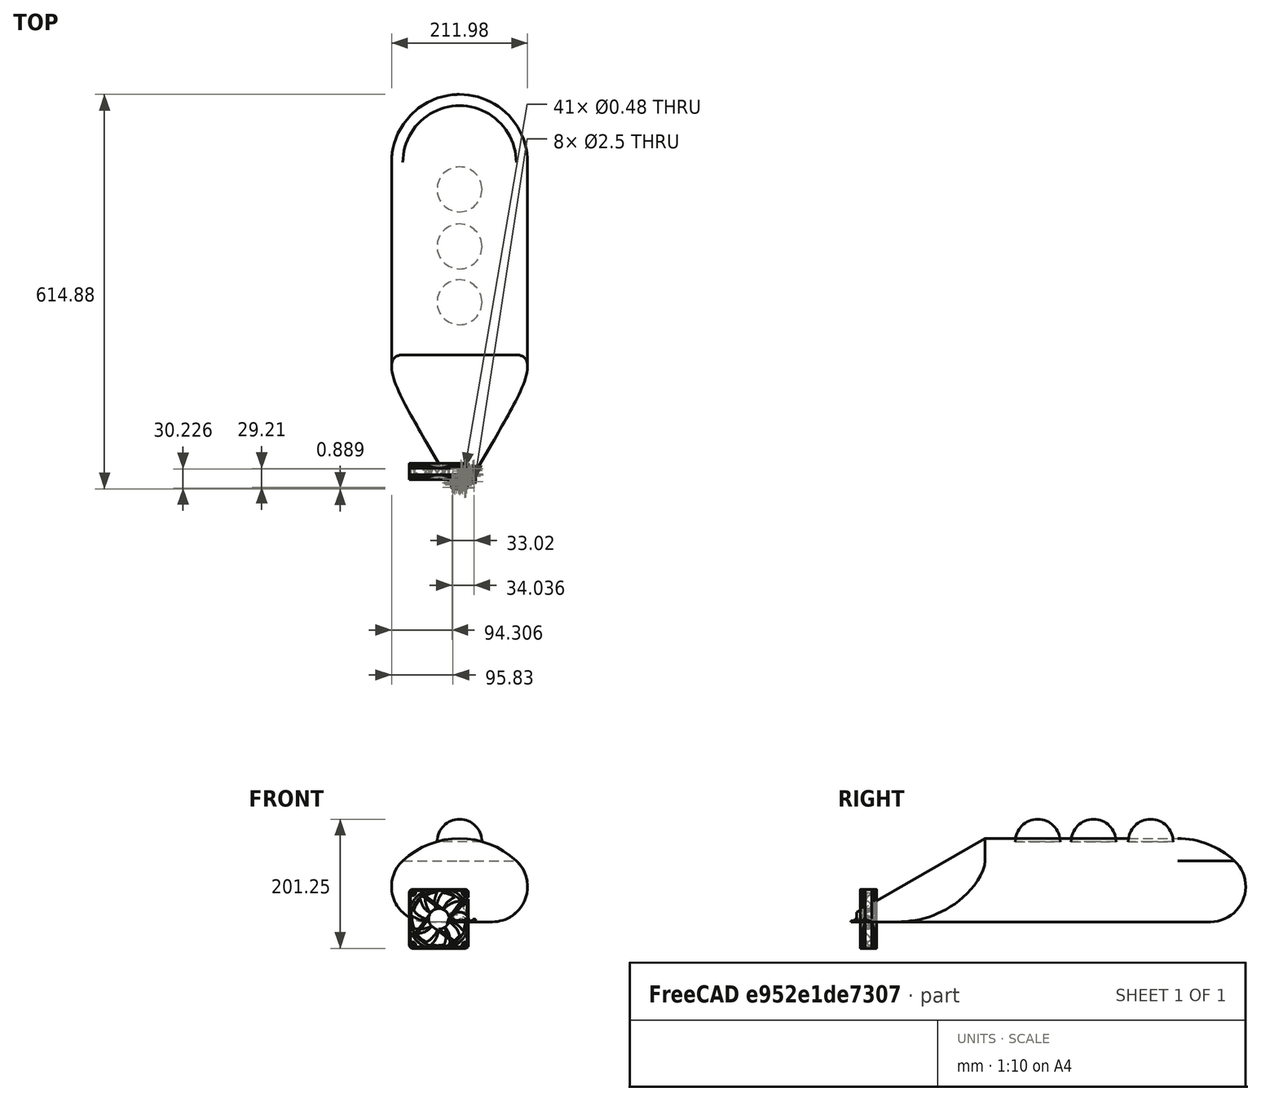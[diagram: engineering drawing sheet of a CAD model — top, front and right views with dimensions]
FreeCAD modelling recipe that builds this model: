
FCSTD DOCUMENT  (FreeCAD 0.21R33668 +7 (Git))
Label: CarNode
License: All rights reserved
LicenseURL: https://en.wikipedia.org/wiki/All_rights_reserved
objects: Part::Feature×52, Part::Box×43, Part::MultiFuse×10, App::Part×10, Part::Sphere×5, Part::Mirroring×3, Part::Cylinder×2, Part::Cone×1, Part::Fillet×1, Mesh::Feature×1, Part::Compound×1
note: 118 computed .brp shape members not serialized (recipe doc carries the construction recipe); baked Part::Feature solids carry a one-line shape summary decoded from their .brp

FEATURE [Part::Cone] Cone
  Angle = 180
  AttacherType = Attacher::AttachEngine3D
  Height = 200
  Placement = pos=(0,0,0) rot=(0,0.707107,0.707107;3.14159rad)
  Radius1 = 15
  Radius2 = 130
FEATURE [Part::Cylinder] Cylinder
  Angle = 180
  AttacherType = Attacher::AttachEngine3D
  FirstAngle = 0
  Height = 300
  Placement = pos=(0,500,-1.11e-13) rot=(1,0,0;1.5708rad)
  Radius = 130
  SecondAngle = 0
FEATURE [Part::Sphere] Sphere
  Angle1 = -90
  Angle2 = 0
  Angle3 = 180
  AttacherType = Attacher::AttachEngine3D
  Placement = pos=(0,500,1.11e-13) rot=(1,0,0;1.5708rad)
  Radius = 130
FEATURE [Part::Sphere] Sphere001
  Angle1 = -90
  Angle2 = 0
  Angle3 = 360
  AttacherType = Attacher::AttachEngine3D
  Placement = pos=(0,282,125) rot=(1,0,0;3.14159rad)
  Radius = 35
FEATURE [Part::Sphere] Sphere002
  Angle1 = -90
  Angle2 = 0
  Angle3 = 360
  AttacherType = Attacher::AttachEngine3D
  Placement = pos=(0,369,125) rot=(1,0,0;3.14159rad)
  Radius = 35
FEATURE [Part::Sphere] Sphere003
  Angle1 = -90
  Angle2 = 0
  Angle3 = 360
  AttacherType = Attacher::AttachEngine3D
  Placement = pos=(0,458,125) rot=(1,0,0;3.14159rad)
  Radius = 35
FEATURE [Part::Cylinder] Cylinder001
  Angle = 360
  AttacherType = Attacher::AttachEngine3D
  FirstAngle = 0
  Height = 180
  Placement = pos=(0,59,90) rot=(-1,0,0;1.5708rad)
  Radius = 35
  SecondAngle = 0
FEATURE [Part::Sphere] Sphere004
  Angle1 = -90
  Angle2 = 0
  Angle3 = 360
  AttacherType = Attacher::AttachEngine3D
  Placement = pos=(0,59,90) rot=(-1,0,0;1.5708rad)
  Radius = 35
FEATURE [Part::MultiFuse] Fusion
  Shapes = -> [Cone,Cylinder,Sphere]
FEATURE [Part::Fillet] Fillet
  Base = -> Fusion
  Edges = 1 edges r=55: [Edge6]
FEATURE [Part::Box] Box  label="Cube"
  AttacherType = Attacher::AttachEngine3D
  Height = 100
  Length = 30
  Placement = pos=(105,177,0) rot=(-0.568128,-0.159475,0.80734;4.12456rad)
  Width = 2.5
FEATURE [Part::Box] Box001  label="Cube001"
  AttacherType = Attacher::AttachEngine3D
  Height = 100
  Length = 30
  Placement = pos=(105,186,0) rot=(-0.568128,-0.159475,0.80734;4.12456rad)
  Width = 2.5
FEATURE [Part::Box] Box002  label="Cube002"
  AttacherType = Attacher::AttachEngine3D
  Height = 100
  Length = 30
  Placement = pos=(105,195,0) rot=(-0.568128,-0.159475,0.80734;4.12456rad)
  Width = 2.5
FEATURE [Part::Box] Box003  label="Cube003"
  AttacherType = Attacher::AttachEngine3D
  Height = 100
  Length = 30
  Placement = pos=(105,204,0) rot=(-0.568128,-0.159475,0.80734;4.12456rad)
  Width = 2.5
FEATURE [Part::Box] Box004  label="Cube004"
  AttacherType = Attacher::AttachEngine3D
  Height = 100
  Length = 30
  Placement = pos=(105,213,0) rot=(-0.568128,-0.159475,0.80734;4.12456rad)
  Width = 2.5
FEATURE [Part::Box] Box005  label="Cube005"
  AttacherType = Attacher::AttachEngine3D
  Height = 100
  Length = 30
  Placement = pos=(105,222,0) rot=(-0.568128,-0.159475,0.80734;4.12456rad)
  Width = 2.5
FEATURE [Part::Box] Box006  label="Cube006"
  AttacherType = Attacher::AttachEngine3D
  Height = 100
  Length = 30
  Placement = pos=(105,231,0) rot=(-0.568128,-0.159475,0.80734;4.12456rad)
  Width = 2.5
FEATURE [Part::MultiFuse] Fusion001  label="Vent"
  Shapes = -> [Box,Box001,Box002,Box003,Box004,Box005,Box006]
FEATURE [Part::Box] Box007  label="Cube007"
  AttacherType = Attacher::AttachEngine3D
  Height = 100
  Length = 30
  Placement = pos=(105,177,0) rot=(-0.568128,-0.159475,0.80734;4.12456rad)
  Width = 2.5
FEATURE [Part::Box] Box008  label="Cube008"
  AttacherType = Attacher::AttachEngine3D
  Height = 100
  Length = 30
  Placement = pos=(105,186,0) rot=(-0.568128,-0.159475,0.80734;4.12456rad)
  Width = 2.5
FEATURE [Part::Box] Box009  label="Cube009"
  AttacherType = Attacher::AttachEngine3D
  Height = 100
  Length = 30
  Placement = pos=(105,195,0) rot=(-0.568128,-0.159475,0.80734;4.12456rad)
  Width = 2.5
FEATURE [Part::Box] Box010  label="Cube010"
  AttacherType = Attacher::AttachEngine3D
  Height = 100
  Length = 30
  Placement = pos=(105,204,0) rot=(-0.568128,-0.159475,0.80734;4.12456rad)
  Width = 2.5
FEATURE [Part::Box] Box011  label="Cube011"
  AttacherType = Attacher::AttachEngine3D
  Height = 100
  Length = 30
  Placement = pos=(105,213,0) rot=(-0.568128,-0.159475,0.80734;4.12456rad)
  Width = 2.5
FEATURE [Part::Box] Box012  label="Cube012"
  AttacherType = Attacher::AttachEngine3D
  Height = 100
  Length = 30
  Placement = pos=(105,222,0) rot=(-0.568128,-0.159475,0.80734;4.12456rad)
  Width = 2.5
FEATURE [Part::Box] Box013  label="Cube013"
  AttacherType = Attacher::AttachEngine3D
  Height = 100
  Length = 30
  Placement = pos=(105,231,0) rot=(-0.568128,-0.159475,0.80734;4.12456rad)
  Width = 2.5
FEATURE [Part::MultiFuse] Fusion002  label="Vent001"
  Placement = pos=(0,101,11) rot=(0,0,1;0rad)
  Shapes = -> [Box007,Box008,Box009,Box010,Box011,Box012,Box013]
FEATURE [Part::Box] Box014  label="Cube014"
  AttacherType = Attacher::AttachEngine3D
  Height = 100
  Length = 30
  Placement = pos=(105,177,0) rot=(-0.568128,-0.159475,0.80734;4.12456rad)
  Width = 2.5
FEATURE [Part::Box] Box015  label="Cube015"
  AttacherType = Attacher::AttachEngine3D
  Height = 100
  Length = 30
  Placement = pos=(105,186,0) rot=(-0.568128,-0.159475,0.80734;4.12456rad)
  Width = 2.5
FEATURE [Part::Box] Box016  label="Cube016"
  AttacherType = Attacher::AttachEngine3D
  Height = 100
  Length = 30
  Placement = pos=(105,195,0) rot=(-0.568128,-0.159475,0.80734;4.12456rad)
  Width = 2.5
FEATURE [Part::Box] Box017  label="Cube017"
  AttacherType = Attacher::AttachEngine3D
  Height = 100
  Length = 30
  Placement = pos=(105,204,0) rot=(-0.568128,-0.159475,0.80734;4.12456rad)
  Width = 2.5
FEATURE [Part::Box] Box018  label="Cube018"
  AttacherType = Attacher::AttachEngine3D
  Height = 100
  Length = 30
  Placement = pos=(105,213,0) rot=(-0.568128,-0.159475,0.80734;4.12456rad)
  Width = 2.5
FEATURE [Part::Box] Box019  label="Cube019"
  AttacherType = Attacher::AttachEngine3D
  Height = 100
  Length = 30
  Placement = pos=(105,222,0) rot=(-0.568128,-0.159475,0.80734;4.12456rad)
  Width = 2.5
FEATURE [Part::Box] Box020  label="Cube020"
  AttacherType = Attacher::AttachEngine3D
  Height = 100
  Length = 30
  Placement = pos=(105,231,0) rot=(-0.568128,-0.159475,0.80734;4.12456rad)
  Width = 2.5
FEATURE [Part::MultiFuse] Fusion003  label="Vent002"
  Placement = pos=(0,196,11) rot=(0,0,1;0rad)
  Shapes = -> [Box014,Box015,Box016,Box017,Box018,Box019,Box020]
FEATURE [Part::Box] Box021  label="Cube021"
  AttacherType = Attacher::AttachEngine3D
  Height = 100
  Length = 30
  Placement = pos=(105,177,0) rot=(-0.568128,-0.159475,0.80734;4.12456rad)
  Width = 2.5
FEATURE [Part::Box] Box022  label="Cube022"
  AttacherType = Attacher::AttachEngine3D
  Height = 100
  Length = 30
  Placement = pos=(105,186,0) rot=(-0.568128,-0.159475,0.80734;4.12456rad)
  Width = 2.5
FEATURE [Part::Box] Box023  label="Cube023"
  AttacherType = Attacher::AttachEngine3D
  Height = 100
  Length = 30
  Placement = pos=(105,195,0) rot=(-0.568128,-0.159475,0.80734;4.12456rad)
  Width = 2.5
FEATURE [Part::Box] Box024  label="Cube024"
  AttacherType = Attacher::AttachEngine3D
  Height = 100
  Length = 30
  Placement = pos=(105,204,0) rot=(-0.568128,-0.159475,0.80734;4.12456rad)
  Width = 2.5
FEATURE [Part::Box] Box025  label="Cube025"
  AttacherType = Attacher::AttachEngine3D
  Height = 100
  Length = 30
  Placement = pos=(105,213,0) rot=(-0.568128,-0.159475,0.80734;4.12456rad)
  Width = 2.5
FEATURE [Part::Box] Box026  label="Cube026"
  AttacherType = Attacher::AttachEngine3D
  Height = 100
  Length = 30
  Placement = pos=(105,222,0) rot=(-0.568128,-0.159475,0.80734;4.12456rad)
  Width = 2.5
FEATURE [Part::Box] Box027  label="Cube027"
  AttacherType = Attacher::AttachEngine3D
  Height = 100
  Length = 30
  Placement = pos=(105,231,0) rot=(-0.568128,-0.159475,0.80734;4.12456rad)
  Width = 2.5
FEATURE [Part::MultiFuse] Fusion004  label="Vent003"
  Shapes = -> [Box021,Box022,Box023,Box024,Box025,Box026,Box027]
FEATURE [Part::Mirroring] Part__Mirroring  label="Vent003 (Mirror #1)"
  Base = (0,0,0)
  Normal = (1,0,0)
  Source = -> Fusion004
FEATURE [Part::MultiFuse] Fusion005  label="Vent01_both"
  Shapes = -> [Fusion001,Part__Mirroring]
FEATURE [Part::Box] Box028  label="Cube028"
  AttacherType = Attacher::AttachEngine3D
  Height = 100
  Length = 30
  Placement = pos=(105,177,0) rot=(-0.568128,-0.159475,0.80734;4.12456rad)
  Width = 2.5
FEATURE [Part::Box] Box029  label="Cube029"
  AttacherType = Attacher::AttachEngine3D
  Height = 100
  Length = 30
  Placement = pos=(105,186,0) rot=(-0.568128,-0.159475,0.80734;4.12456rad)
  Width = 2.5
FEATURE [Part::Box] Box030  label="Cube030"
  AttacherType = Attacher::AttachEngine3D
  Height = 100
  Length = 30
  Placement = pos=(105,195,0) rot=(-0.568128,-0.159475,0.80734;4.12456rad)
  Width = 2.5
FEATURE [Part::Box] Box031  label="Cube031"
  AttacherType = Attacher::AttachEngine3D
  Height = 100
  Length = 30
  Placement = pos=(105,204,0) rot=(-0.568128,-0.159475,0.80734;4.12456rad)
  Width = 2.5
FEATURE [Part::Box] Box032  label="Cube032"
  AttacherType = Attacher::AttachEngine3D
  Height = 100
  Length = 30
  Placement = pos=(105,213,0) rot=(-0.568128,-0.159475,0.80734;4.12456rad)
  Width = 2.5
FEATURE [Part::Box] Box033  label="Cube033"
  AttacherType = Attacher::AttachEngine3D
  Height = 100
  Length = 30
  Placement = pos=(105,222,0) rot=(-0.568128,-0.159475,0.80734;4.12456rad)
  Width = 2.5
FEATURE [Part::Box] Box034  label="Cube034"
  AttacherType = Attacher::AttachEngine3D
  Height = 100
  Length = 30
  Placement = pos=(105,231,0) rot=(-0.568128,-0.159475,0.80734;4.12456rad)
  Width = 2.5
FEATURE [Part::MultiFuse] Fusion006  label="Vent004"
  Placement = pos=(0,101,11) rot=(0,0,1;0rad)
  Shapes = -> [Box028,Box029,Box030,Box031,Box032,Box033,Box034]
FEATURE [Part::Mirroring] Part__Mirroring001  label="Vent004 (Mirror #2)"
  Base = (0,0,0)
  Normal = (1,0,0)
  Source = -> Fusion006
FEATURE [Part::MultiFuse] Fusion007  label="Vent02_both"
  Shapes = -> [Fusion002,Part__Mirroring001]
FEATURE [Part::Box] Box035  label="Cube035"
  AttacherType = Attacher::AttachEngine3D
  Height = 100
  Length = 30
  Placement = pos=(105,177,0) rot=(-0.568128,-0.159475,0.80734;4.12456rad)
  Width = 2.5
FEATURE [Part::Box] Box036  label="Cube036"
  AttacherType = Attacher::AttachEngine3D
  Height = 100
  Length = 30
  Placement = pos=(105,186,0) rot=(-0.568128,-0.159475,0.80734;4.12456rad)
  Width = 2.5
FEATURE [Part::Box] Box037  label="Cube037"
  AttacherType = Attacher::AttachEngine3D
  Height = 100
  Length = 30
  Placement = pos=(105,195,0) rot=(-0.568128,-0.159475,0.80734;4.12456rad)
  Width = 2.5
FEATURE [Part::Box] Box038  label="Cube038"
  AttacherType = Attacher::AttachEngine3D
  Height = 100
  Length = 30
  Placement = pos=(105,204,0) rot=(-0.568128,-0.159475,0.80734;4.12456rad)
  Width = 2.5
FEATURE [Part::Box] Box039  label="Cube039"
  AttacherType = Attacher::AttachEngine3D
  Height = 100
  Length = 30
  Placement = pos=(105,213,0) rot=(-0.568128,-0.159475,0.80734;4.12456rad)
  Width = 2.5
FEATURE [Part::Box] Box040  label="Cube040"
  AttacherType = Attacher::AttachEngine3D
  Height = 100
  Length = 30
  Placement = pos=(105,222,0) rot=(-0.568128,-0.159475,0.80734;4.12456rad)
  Width = 2.5
FEATURE [Part::Box] Box041  label="Cube041"
  AttacherType = Attacher::AttachEngine3D
  Height = 100
  Length = 30
  Placement = pos=(105,231,0) rot=(-0.568128,-0.159475,0.80734;4.12456rad)
  Width = 2.5
FEATURE [Part::MultiFuse] Fusion008  label="Vent005"
  Placement = pos=(0,196,11) rot=(0,0,1;0rad)
  Shapes = -> [Box035,Box036,Box037,Box038,Box039,Box040,Box041]
FEATURE [Part::Mirroring] Part__Mirroring002  label="Vent005 (Mirror #3)"
  Base = (0,0,0)
  Normal = (1,0,0)
  Source = -> Fusion008
FEATURE [Part::MultiFuse] Fusion009  label="Vent03_both"
  Shapes = -> [Fusion003,Part__Mirroring002]
FEATURE [Mesh::Feature] Odroid_H004  label="Odroid-H004"
  Placement = pos=(-55,360,48) rot=(0,0,1;4.71239rad)
FEATURE [Part::Box] Box042  label="as7265x"
  AttacherType = Attacher::AttachEngine3D
  Height = 2
  Length = 36
  Placement = pos=(-75,-170.5,110) rot=(0,0,1;0rad)
  Width = 41
FEATURE [Part::Feature] Part__Feature040  label="CeramicBody (1)"
  shape: bbox 1.8 x 1.23 x 1.23 mm, 10 faces (baked)
FEATURE [Part::Feature] Part__Feature104  label="ips7100"
  Placement = pos=(-24,0,222) rot=(0.999993,-0.003655,0;3.14159rad)
  shape: bbox 48.14 x 14.05 x 44.14 mm, 1935 faces (baked)
FEATURE [Part::Compound] Compound  label="ips7100s"
  Links = -> [Part__Feature104]
  Placement = pos=(24,-180,25) rot=(0,0,1;0.006109rad)
FEATURE [Part::Feature] Part__Feature126  label="scd30"
  Placement = pos=(-1e-15,-110,40) rot=(1,0,0;3.14159rad)
  shape: bbox 35.11 x 7.027 x 23.02 mm, 2292 faces, 25 solids (baked)
FEATURE [Part::Feature] Part__Feature127  label="Board"
  shape: bbox 25.4 x 25.4 x 1.57 mm, 211 faces (baked)
FEATURE [Part::Feature] Part__Feature128  label="QFN24_4MM"
  Placement = pos=(12.1412,14.4526,1.57) rot=(0,0,1;3.92699rad)
  shape: bbox 5.657 x 5.657 x 0.9 mm, 172 faces (baked)
FEATURE [Part::Feature] Part__Feature129  label="Part 5"
  shape: bbox 0.48 x 0.6603 x 0.6 mm, 14 faces (baked)
FEATURE [Part::Feature] Part__Feature130  label="Part 6"
  shape: bbox 0.48 x 0.6603 x 0.6 mm, 14 faces (baked)
FEATURE [Part::Feature] Part__Feature131  label="Part 4"
  shape: bbox 0.48 x 0.6603 x 0.6 mm, 14 faces (baked)
FEATURE [Part::Feature] Part__Feature132  label="Part 3"
  shape: bbox 0.48 x 0.6603 x 0.6 mm, 14 faces (baked)
FEATURE [Part::Feature] Part__Feature133  label="Part 010"
  shape: bbox 0.48 x 0.6603 x 0.6 mm, 14 faces (baked)
FEATURE [Part::Feature] Part__Feature134  label="Part 011"
  shape: bbox 3 x 1.4 x 1 mm, 10 faces (baked)
FEATURE [Part::Feature] Part__Feature135  label="Pin1"
  shape: bbox 0.6224 x 1.252 x 1.252 mm, 37 faces (baked)
FEATURE [Part::Feature] Part__Feature136  label="Pin2"
  shape: bbox 0.6224 x 1.252 x 1.252 mm, 37 faces (baked)
FEATURE [Part::Feature] Part__Feature137  label="CeramicBody"
  shape: bbox 1.8 x 1.23 x 1.23 mm, 10 faces (baked)
FEATURE [Part::Feature] Part__Feature138  label="0603-NO (1)"
  Placement = pos=(23.241,6.223,1.57) rot=(0,0,1;0rad)
  shape: bbox 1.7 x 0.9 x 0.55 mm, 52 faces, 3 solids (baked)
FEATURE [Part::Feature] Part__Feature139  label="0603-NO (2)"
  Placement = pos=(13.3858,8.4328,1.57) rot=(0,0,1;0rad)
  shape: bbox 1.7 x 0.9 x 0.55 mm, 52 faces, 3 solids (baked)
FEATURE [Part::Feature] Part__Feature140  label="0603-NO (3)"
  Placement = pos=(1.905,18.923,1.57) rot=(0,0,1;3.14159rad)
  shape: bbox 1.7 x 0.9 x 0.55 mm, 52 faces, 3 solids (baked)
FEATURE [Part::Feature] Part__Feature141  label="Pin1 (1)"
  shape: bbox 0.6224 x 1.252 x 1.252 mm, 37 faces (baked)
FEATURE [Part::Feature] Part__Feature142  label="Pin2 (1)"
  shape: bbox 0.6224 x 1.252 x 1.252 mm, 37 faces (baked)
FEATURE [Part::Feature] Part__Feature143  label="Pin1 (2)"
  shape: bbox 0.6224 x 1.252 x 1.252 mm, 37 faces (baked)
FEATURE [Part::Feature] Part__Feature144  label="Pin2 (2)"
  shape: bbox 0.6224 x 1.252 x 1.252 mm, 37 faces (baked)
FEATURE [Part::Feature] Part__Feature145  label="CeramicBody (2)"
  shape: bbox 1.8 x 1.23 x 1.23 mm, 10 faces (baked)
FEATURE [Part::Feature] Part__Feature146  label="CHIPLED_0603_NOOUTLINE"
  Placement = pos=(23.368,8.509,1.57) rot=(0,0,1;1.5708rad)
  shape: bbox 1.616 x 0.8 x 0.4 mm, 133 faces (baked)
FEATURE [Part::Feature] Part__Feature147  label="CHIPLED_0603_NOOUTLINE (1)"
  Placement = pos=(1.905,16.764,1.57) rot=(0,0,-1;1.5708rad)
  shape: bbox 1.616 x 0.8 x 0.4 mm, 133 faces (baked)
FEATURE [Part::Feature] Part__Feature148  label="JST_SH4"
  Placement = pos=(22.86,12.7,1.57) rot=(0,0,1;1.5708rad)
  shape: bbox 4.95 x 6 x 2.96 mm, 229 faces, 7 solids (baked)
FEATURE [Part::Feature] Part__Feature149  label="JST_SH4 (1)"
  Placement = pos=(2.54,12.7,1.57) rot=(0,0,-1;1.5708rad)
  shape: bbox 4.95 x 6 x 2.96 mm, 229 faces, 7 solids (baked)
FEATURE [Part::Feature] Part__Feature150  label="NEO3535_REVERSE"
  Placement = pos=(12.7,23.114,0) rot=(0,1,0;3.14159rad)
  shape: bbox 5.88 x 2.8 x 1.78 mm, 41 faces, 5 solids (baked)
FEATURE [Part::Feature] Part__Feature151  label="RESPACK_4X0603"
  Placement = pos=(22.86,18.415,1.57) rot=(0,0,1;3.14159rad)
  shape: bbox 3.2 x 1.6 x 0.61 mm, 172 faces (baked)
FEATURE [Part::Feature] Part__Feature152  label="SOT363"
  Placement = pos=(17.399,12.192,1.57) rot=(0,0,-1;1.5708rad)
  shape: bbox 2.208 x 2.208 x 1.121 mm, 178 faces, 4 solids (baked)
FEATURE [Part::Feature] Part__Feature153  label="Printed Circuit Board001"
  shape: bbox 25.4 x 17.78 x 1.6 mm, 42 faces (baked)
FEATURE [Part::Feature] Part__Feature154  label="EAHC2835WD007"
  shape: bbox 3.513 x 2.813 x 0.7485 mm, 108 faces, 4 solids (baked)
FEATURE [Part::Feature] Part__Feature155  label="AS7341 v003"
  Placement = pos=(0,-0.339822,1.6) rot=(0,0,1;0rad)
  shape: bbox 2 x 3.1 x 1.1 mm, 267 faces, 26 solids (baked)
FEATURE [Part::Feature] Part__Feature156  label="CAPC-0805-T0.95-BN v004"
  Placement = pos=(-5.01759,-3.15294,1.6) rot=(0,0,1;0rad)
  shape: bbox 2.1 x 1.35 x 0.95 mm, 42 faces (baked)
FEATURE [Part::Feature] Part__Feature157  label="CAPC-0805-T0.95-BN v005"
  Placement = pos=(-5.48627,2.66154,1.6) rot=(0,0,-1;1.5708rad)
  shape: bbox 1.35 x 2.1 x 0.95 mm, 42 faces (baked)
FEATURE [Part::Feature] Part__Feature158  label="CAPC-0805-T0.95-BN v006"
  Placement = pos=(-3.43627,2.66154,1.6) rot=(0,0,-1;1.5708rad)
  shape: bbox 1.35 x 2.1 x 0.95 mm, 42 faces (baked)
FEATURE [Part::Feature] Part__Feature159  label="CAPC-0603-T0.9-BN v002"
  Placement = pos=(-1.69987,-3.28475,1.6) rot=(0,0,1;0rad)
  shape: bbox 1.7 x 0.9 x 0.9 mm, 42 faces (baked)
FEATURE [Part::Feature] Part__Feature160  label="BODY_MF06A001"
  Placement = pos=(0,0,0.762) rot=(0.57735,-0.57735,-0.57735;2.0944rad)
  shape: bbox 1.601 x 2.921 x 1.016 mm, 42 faces (baked)
FEATURE [Part::Feature] Part__Feature161  label="LEAD_MF06A006"
  Placement = pos=(-0.9652,-0.9525,0.1016) rot=(0.57735,-0.57735,-0.57735;2.0944rad)
  shape: bbox 0.6223 x 0.3749 x 0.8636 mm, 14 faces (baked)
FEATURE [Part::Feature] Part__Feature162  label="LEAD_MF06A007"
  Placement = pos=(-0.9652,0,0.1016) rot=(0.57735,-0.57735,-0.57735;2.0944rad)
  shape: bbox 0.6223 x 0.3749 x 0.8636 mm, 14 faces (baked)
FEATURE [Part::Feature] Part__Feature163  label="LEAD_MF06A008"
  Placement = pos=(-0.9652,0.9525,0.1016) rot=(0.57735,-0.57735,-0.57735;2.0944rad)
  shape: bbox 0.6223 x 0.3749 x 0.8636 mm, 14 faces (baked)
FEATURE [Part::Feature] Part__Feature164  label="LEAD_MF06A009"
  Placement = pos=(0.9652,-0.9525,0.1016) rot=(0.57735,0.57735,0.57735;2.0944rad)
  shape: bbox 0.6223 x 0.3749 x 0.8636 mm, 14 faces (baked)
FEATURE [Part::Feature] Part__Feature165  label="LEAD_MF06A010"
  Placement = pos=(0.9652,0,0.1016) rot=(0.57735,0.57735,0.57735;2.0944rad)
  shape: bbox 0.6223 x 0.3749 x 0.8636 mm, 14 faces (baked)
FEATURE [Part::Feature] Part__Feature166  label="LEAD_MF06A011"
  Placement = pos=(0.9652,0.9525,0.1016) rot=(0.57735,0.57735,0.57735;2.0944rad)
  shape: bbox 0.6223 x 0.3749 x 0.8636 mm, 14 faces (baked)
FEATURE [Part::Feature] Part__Feature167  label="SOT363 v003"
  Placement = pos=(4.97054,-0.645171,1.675) rot=(0,0,1;3.14159rad)
  shape: bbox 2.1 x 2 x 1.1 mm, 94 faces, 7 solids (baked)
FEATURE [Part::Feature] Part__Feature168  label="LED 0603 single color v002"
  Placement = pos=(-9.18406,3.72778,1.60762) rot=(0,0,1;1.5708rad)
  shape: bbox 1.961 x 0.7932 x 0.7145 mm, 63 faces, 5 solids (baked)
FEATURE [Part::Feature] Part__Feature169  label="RESC-0603 v003"
  Placement = pos=(4.83432,-3.67461,1.6) rot=(0,0,1;0rad)
  shape: bbox 1.7 x 0.9 x 0.55 mm, 52 faces, 3 solids (baked)
FEATURE [Part::Feature] Part__Feature170  label="RESC-0603 v004"
  Placement = pos=(-7.14949,3.61248,1.6) rot=(0,0,-1;1.5708rad)
  shape: bbox 0.9 x 1.7 x 0.55 mm, 52 faces, 3 solids (baked)
FEATURE [Part::Feature] Part__Feature171  label="YC164_RESPACK v002"
  Placement = pos=(2.99591,1.52916,1.6) rot=(0,0,1;0rad)
  shape: bbox 3.2 x 1.6 x 0.61 mm, 172 faces (baked)
FEATURE [Part::Feature] Part__Feature172  label="qwicc v004"
  Placement = pos=(-10.8364,0.0607456,1.65) rot=(0,0,-1;1.5708rad)
  shape: bbox 4.95 x 6 x 2.96 mm, 229 faces, 7 solids (baked)
FEATURE [Part::Feature] Part__Feature173  label="qwicc v005"
  Placement = pos=(10.8256,0.00556102,1.65) rot=(0,0,1;1.5708rad)
  shape: bbox 4.95 x 6 x 2.96 mm, 229 faces, 7 solids (baked)
FEATURE [Part::Feature] Part__Feature198  label="F9 body"
  Placement = pos=(-78.1983,5.70939,50.7544) rot=(0,0,1;0rad)
  shape: bbox 118.8 x 26.53 x 118.8 mm, 173 faces (baked)
FEATURE [Part::Feature] Part__Feature199  label="F9 fan"
  Placement = pos=(-74.2115,10.4094,-44.9134) rot=(0,-1,0;1.65409rad)
  shape: bbox 98.04 x 20 x 97.21 mm, 60 faces (baked)
FEATURE [App::Part] F9  label="fan"
  Group = -> [Part__Feature198,Part__Feature199]
  Origin = -> Origin
  Placement = pos=(41.25,309,112.5) rot=(1,0,0;4.71239rad)
FEATURE [App::Part] _603_NO  label="0603-NO"
  Group = -> [Part__Feature135,Part__Feature136,Part__Feature137]
  Origin = -> Origin012
  Placement = pos=(16.51,8.382,1.57) rot=(0,0,1;0rad)
FEATURE [App::Part] _6700497  label="36700497"
  Group = -> [Part__Feature129,Part__Feature130,Part__Feature131,Part__Feature132,Part__Feature133,Part__Feature134]
  Origin = -> Origin010
  Placement = pos=(0,0,0) rot=(0,0,1;3.14159rad)
FEATURE [App::Part] SOT23_5  label="SOT23-5"
  Group = -> [_6700497]
  Origin = -> Origin011
  Placement = pos=(2.54,6.985,1.57) rot=(0,0,1;3.14159rad)
FEATURE [App::Part] _805_NO  label="0805-NO"
  Group = -> [Part__Feature141,Part__Feature142,Part__Feature040]
  Origin = -> Origin013
  Placement = pos=(7.874,13.589,1.57) rot=(0,0,1;1.5708rad)
FEATURE [App::Part] _805_NO__1_  label="0805-NO (1)"
  Group = -> [Part__Feature143,Part__Feature144,Part__Feature145]
  Origin = -> Origin014
  Placement = pos=(12.827,6.223,1.57) rot=(0,0,1;3.14159rad)
FEATURE [App::Part] Packages
  Group = -> [Part__Feature128,SOT23_5,_603_NO,Part__Feature138,Part__Feature139,Part__Feature140,_805_NO,_805_NO__1_,Part__Feature146,Part__Feature147,Part__Feature148,Part__Feature149,Part__Feature150,Part__Feature151,Part__Feature152]
  Origin = -> Origin015
FEATURE [App::Part] Adafruit_I2C_QT_Rotary_Encoder_v2  label="gps"
  Group = -> [Part__Feature127,Packages]
  Origin = -> Origin016
  Placement = pos=(-12.7,-163,95) rot=(0,0,1;0rad)
FEATURE [App::Part] sot_23_6_v003  label="sot-23-6 v003"
  Group = -> [Part__Feature160,Part__Feature161,Part__Feature162,Part__Feature163,Part__Feature164,Part__Feature165,Part__Feature166]
  Origin = -> Origin017
  Placement = pos=(-4.47945,-0.603742,1.69152) rot=(0,0,1;0rad)
FEATURE [App::Part] Adafruit_AS7341_STEMMA_QT_v003  label="bme280"
  Group = -> [Part__Feature153,Part__Feature154,Part__Feature155,Part__Feature156,Part__Feature157,Part__Feature158,Part__Feature159,sot_23_6_v003,Part__Feature167,Part__Feature168,Part__Feature169,Part__Feature170,Part__Feature171,Part__Feature172,Part__Feature173]
  Origin = -> Origin018
  Placement = pos=(30,-149.75,45) rot=(0.57735,-0.57735,0.57735;4.18879rad)
